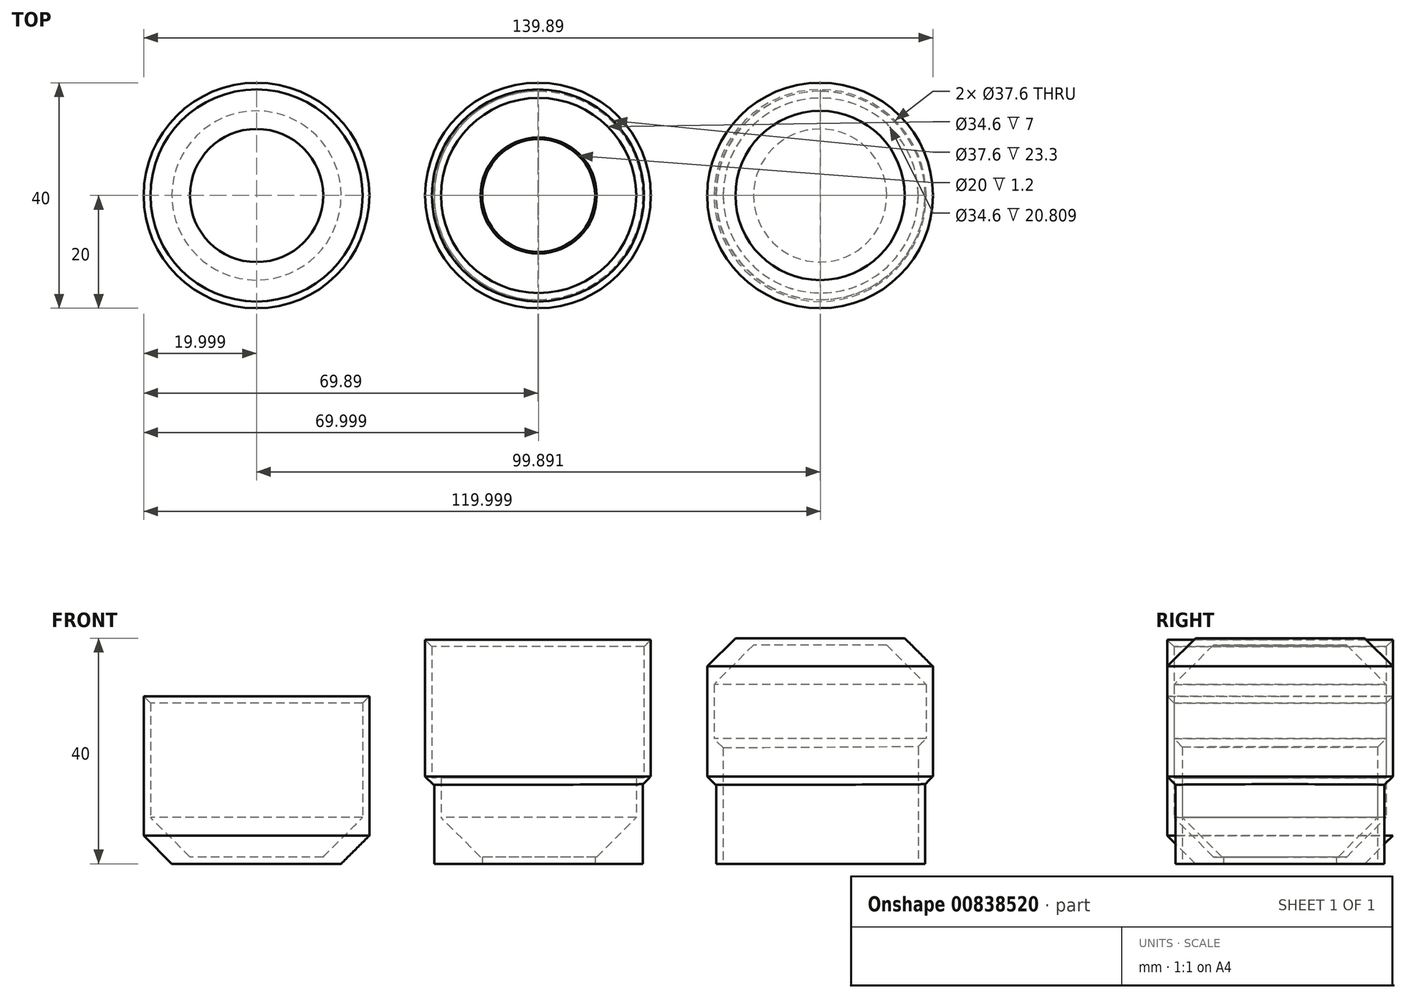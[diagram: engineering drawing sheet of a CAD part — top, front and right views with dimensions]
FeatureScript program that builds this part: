
annotation { "Feature Type Name" : "Feature", "Feature Type Description" : "" }
export const myFeature = defineFeature(function(context is Context, id is Id, definition is map)
    precondition{}
    {
        {
            var Q0;
            Q0=qCreatedBy(makeId("Top.planeOp"),FACE);
            var sketch = newSketch(context, id + "F0", { "sketchPlane" : qUnion([Q0])});
            skCircle(sketch, "E0", {"center": v(-49.9, 0) * mm, "radius": 20 * mm});
            skCircle(sketch, "E1.1.0.0", {"center": v(0.1, 0) * mm, "radius": 20 * mm, "construction": true});
            skCircle(sketch, "E1.2.0.0", {"center": v(50.1, 0) * mm, "radius": 20 * mm, "construction": true});
            skLineSegment(sketch, "E1.direction1", {"start": v(-49.9, 0) * mm, "end": v(0.1, 0) * mm, "construction": true});
            skCircle(sketch, "E2.0", {"center": v(0.1, 0) * mm, "radius": 18.5 * mm});
            skCircle(sketch, "E3.0", {"center": v(50.1, 0) * mm, "radius": 18.5 * mm});
            skCircle(sketch, "E4", {"center": v(0.1, 0) * mm, "radius": 10 * mm});
            skSolve(sketch);
        }
        {
            var Q0;
            Q0=makeQuery(id+"F0.imprint","IMPRINT",FACE,{"disambiguationData":[TD([[makeQuery(id+"F0.imprint","IMPRINT",EDGE,{"derivedFrom":sQuery(id+"F0.wireOp",EDGE,"E0")}),1.0]])]});
            extrude(context, id + "F1", {"entities" : qUnion([Q0]), "depth" : 30 * mm, "offsetDistance" : 25 * mm});
        }
        {
            var Q0;
            Q0=makeQuery(id+"F0.imprint","IMPRINT",FACE,{"disambiguationData":[TD([[makeQuery(id+"F0.imprint","IMPRINT",EDGE,{"derivedFrom":sQuery(id+"F0.wireOp",EDGE,"E2.0")}),1.0]])]});
            var Q1;
            Q1=makeQuery(id+"F0.imprint","IMPRINT",FACE,{"disambiguationData":[TD([[makeQuery(id+"F0.imprint","IMPRINT",EDGE,{"derivedFrom":sQuery(id+"F0.wireOp",EDGE,"E3.0")}),1.0]])]});
            var Q2;
            Q2=makeQuery(id+"F0.imprint","IMPRINT",FACE,{"disambiguationData":[TD([[makeQuery(id+"F0.imprint","IMPRINT",EDGE,{"derivedFrom":sQuery(id+"F0.wireOp",EDGE,"E4")}),1.0]])]});
            extrude(context, id + "F2", {"entities" : qUnion([Q0, Q1, Q2]), "depth" : 15 * mm, "offsetDistance" : 25 * mm});
        }
        {
            var Q0;
            Q0=makeQuery(id+"F2.opExtrude","CAP_FACE",FACE,{"disambiguationData":[OSD([sQuery(id+"F0.wireOp",EDGE,"E2.0")])],"isStart":false});
            var sketch = newSketch(context, id + "F3", { "sketchPlane" : qUnion([Q0])});
            skCircle(sketch, "E5", {"center": v(0, 0) * mm, "radius": 20 * mm});
            skCircle(sketch, "E6", {"center": v(50, 0) * mm, "radius": 20 * mm});
            skSolve(sketch);
        }
        {
            var Q0;
            Q0=makeQuery(id+"F3.imprint","IMPRINT",FACE,{"disambiguationData":[TD([[makeQuery(id+"F3.imprint","IMPRINT",EDGE,{"derivedFrom":sQuery(id+"F3.wireOp",EDGE,"E6")}),1.0]])]});
            var Q1;
            Q1=makeQuery(id+"F3.imprint","IMPRINT",FACE,{"disambiguationData":[TD([[makeQuery(id+"F3.imprint","IMPRINT",EDGE,{"derivedFrom":sQuery(id+"F3.wireOp",EDGE,"E5")}),1.0]])]});
            var Q2;
            Q2=makeQuery(id+"F3.imprint","IMPRINT",FACE,{"disambiguationData":[TD([[makeQuery(id+"F3.imprint","IMPRINT",EDGE,{"derivedFrom":makeQuery(id+"F2.opExtrude","CAP_EDGE",EDGE,{"disambiguationData":[OSD([sQuery(id+"F0.wireOp",EDGE,"E2.0")])],"isStart":false})}),1.0]])]});
            extrude(context, id + "F4", {"entities" : qUnion([Q0, Q1, Q2]), "operationType" : NewBodyOperationType.ADD, "depth" : 25 * mm, "offsetDistance" : 25 * mm, "hasSecondDirection" : true, "secondDirectionOppositeDirection" : true, "secondDirectionDepth" : 1 * mm});
        }
        {
            var Q0;
            Q0=makeQuery(id+"F1.opExtrude","CAP_FACE",FACE,{"disambiguationData":[OSD([sQuery(id+"F0.wireOp",EDGE,"E0")])],"isStart":false});
            var Q1;
            Q1=makeQuery(id+"F4.opExtrude","CAP_FACE",FACE,{"disambiguationData":[OSD([sQuery(id+"F3.wireOp",EDGE,"E5")])],"isStart":false});
            var Q2;
            Q2=makeQuery(id+"F2.opExtrude","CAP_FACE",FACE,{"disambiguationData":[OSD([sQuery(id+"F0.wireOp",EDGE,"E3.0")])],"isStart":true});
            shell(context, id + "F5", {"entities" : qUnion([Q0, Q1, Q2]), "thickness" : 1.2 * mm});
        }
        {
            var Q0;
            Q0=makeQuery(id+"F0.imprint","IMPRINT",FACE,{"disambiguationData":[TD([[makeQuery(id+"F0.imprint","IMPRINT",EDGE,{"derivedFrom":sQuery(id+"F0.wireOp",EDGE,"E4")}),1.0]])]});
            extrude(context, id + "F6", {"entities" : qUnion([Q0]), "operationType" : NewBodyOperationType.REMOVE, "depth" : 25 * mm, "offsetDistance" : 25 * mm});
        }
        {
            var Q0;
            {var subQ0=sQuery(id+"F0.wireOp",EDGE,"E0");Q0=makeQuery(id+"F5.opShell","OFFSET_EDGE",EDGE,{"disambiguationData":[OSD([subQ0]),TDD([makeQuery(id+"F1.opExtrude","CAP_EDGE",EDGE,{"disambiguationData":[OSD([subQ0])],"isStart":true})])]});}
            var Q1;
            Q1=makeQuery(id+"F5.opShell","OFFSET_EDGE",EDGE,{"disambiguationData":[OSD([sQuery(id+"F0.wireOp",EDGE,"E2.0")])]});
            var Q2;
            {var subQ0=sQuery(id+"F3.wireOp",EDGE,"E6");Q2=makeQuery(id+"F5.opShell","OFFSET_FACE",FACE,{"disambiguationData":[OSD([subQ0]),TDD([makeQuery(id+"F4.opExtrude","SWEPT_FACE",FACE,{"disambiguationData":[OSD([subQ0])]})])]});}
            chamfer(context, id + "F7", {"entities" : qUnion([Q0, Q1, Q2]), "width" : 7 * mm, "tangentPropagation" : true});
        }
        {
            var Q0;
            Q0=makeQuery(id+"F4.opExtrude","CAP_EDGE",EDGE,{"disambiguationData":[OSD([sQuery(id+"F3.wireOp",EDGE,"E5")])],"isStart":true});
            var Q1;
            {var subQ0=sQuery(id+"F0.wireOp",EDGE,"E0");Q1=makeQuery(id+"F5.opShell","OFFSET_EDGE",EDGE,{"disambiguationData":[OSD([subQ0]),TDD([makeQuery(id+"F1.opExtrude","CAP_EDGE",EDGE,{"disambiguationData":[OSD([subQ0])],"isStart":false})])]});}
            var Q2;
            Q2=makeQuery(id+"F4.opExtrude","CAP_EDGE",EDGE,{"disambiguationData":[OSD([sQuery(id+"F3.wireOp",EDGE,"E6")])],"isStart":true});
            var Q3;
            {var subQ0=sQuery(id+"F3.wireOp",EDGE,"E5");Q3=makeQuery(id+"F5.opShell","OFFSET_EDGE",EDGE,{"disambiguationData":[OSD([subQ0]),TDD([makeQuery(id+"F4.opExtrude","CAP_EDGE",EDGE,{"disambiguationData":[OSD([subQ0])],"isStart":false})])]});}
            chamfer(context, id + "F8", {"entities" : qUnion([Q0, Q1, Q2, Q3]), "width" : 1.5 * mm, "tangentPropagation" : true});
        }
        {
            var Q0;
            Q0=makeQuery(id+"F1.opExtrude","CAP_EDGE",EDGE,{"disambiguationData":[OSD([sQuery(id+"F0.wireOp",EDGE,"E0")])],"isStart":true});
            var Q1;
            Q1=makeQuery(id+"F4.opExtrude","CAP_EDGE",EDGE,{"disambiguationData":[OSD([sQuery(id+"F3.wireOp",EDGE,"E6")])],"isStart":false});
            chamfer(context, id + "F9", {"entities" : qUnion([Q0, Q1]), "width" : 5 * mm, "tangentPropagation" : true});
        }
    });
